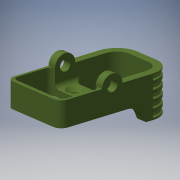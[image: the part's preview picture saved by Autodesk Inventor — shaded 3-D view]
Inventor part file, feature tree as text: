
AUTODESK INVENTOR PART (.ipt)
format: ipt  version: 2018 (Build 220112000, 112)  size: 937,984 bytes
history: native  units: mm
features: sketch x8, extrude x7, fillet x4, plane x2, projected_geometry x2, hole x1, sweep x1, pattern_linear x1
ambient origin geometry x8: Origin, YZ Plane, XZ Plane, XY Plane, X Axis, Y Axis, Z Axis, Center Point
bodies: Solid1 (feature_tree)
feature tree (26):
  extrude  "Extrusion1"  Depth=25.0mm
  extrude  "Extrusion2"  Depth=3.0mm
  sketch  "Sketch3"  dims[d4=15.0mm d5=0.0mm d6=15.0mm]
  extrude  "Extrusion3"  Depth=15.0mm
  extrude  "Extrusion4"  Depth=26.5mm
  extrude  "Extrusion5"  Depth=2.0mm
  hole  "Hole1"  [1 undecoded]
  extrude  "Extrusion6"  Depth=20.5mm
  extrude  "Extrusion7"  Depth=2.0mm
  plane  "Work Plane1"
  sketch  "Sketch7"  dims[d15=4.0mm d17=20.5mm]
  plane  "Work Plane2"
  sweep  "Sweep1"
  pattern_linear  "Rectangular Pattern1"  Spacing1=23.0mm  [1 undecoded]
  fillet  "Fillet1"  Radius=15.0mm
  fillet  "Fillet2"  Radius=1.0mm
  fillet  "Fillet3"  Radius=1.5mm
  fillet  "Fillet4"  Radius=3.0mm
  sketch  "Sketch1"  dims[d0=44.5mm d1=25.0mm]
  sketch  "Sketch2"  dims[d2=8.0mm d3=3.0mm]
  sketch  "Sketch4"  dims[d7=9.0mm d9=26.5mm]
  sketch  "Sketch5"  dims[d10=6.0mm d11=2.0mm]
  sketch  "Sketch6"  dims[d12=15.0mm d13=0.0mm d14=8.0mm]
  sketch  "Sketch8"  dims[d18=3.0mm d19=0.0mm d20=19.0mm d21=17.0mm d22=23.0mm d23=15.0mm d24=1.0mm d25=1.5mm d26=3.0mm d27=3.0mm d28=5.0mm d29=2.0mm d30=15.0mm d31=0.0mm d32=6.5mm d33=0.0mm d34=20.5mm d35=7.5mm d36=10.0mm d37=3.2mm d38=6.0mm d39=6.0mm d40=2.0mm d41=90.0deg d42=5.25mm d43=20.594885mm d44=50.0mm d45=0.0mm d46=3.0mm d47=0.0mm d48=-1.52mm d49=10.75mm d50=1.5mm d51=0.0mm d52=0.0mm d53=50.0mm d55=3.0mm d56=0.2mm d57=0.2mm d58=0.21mm d59=2.0mm]
  projected_geometry  "Project Cut Edges1"
  projected_geometry  "Project Cut Edges2"
note: 2 required parameter values undecoded (feature->parameter linkage not recoverable at this tier; creation-order binding heuristic only, values carry confidence <= 0.55)
